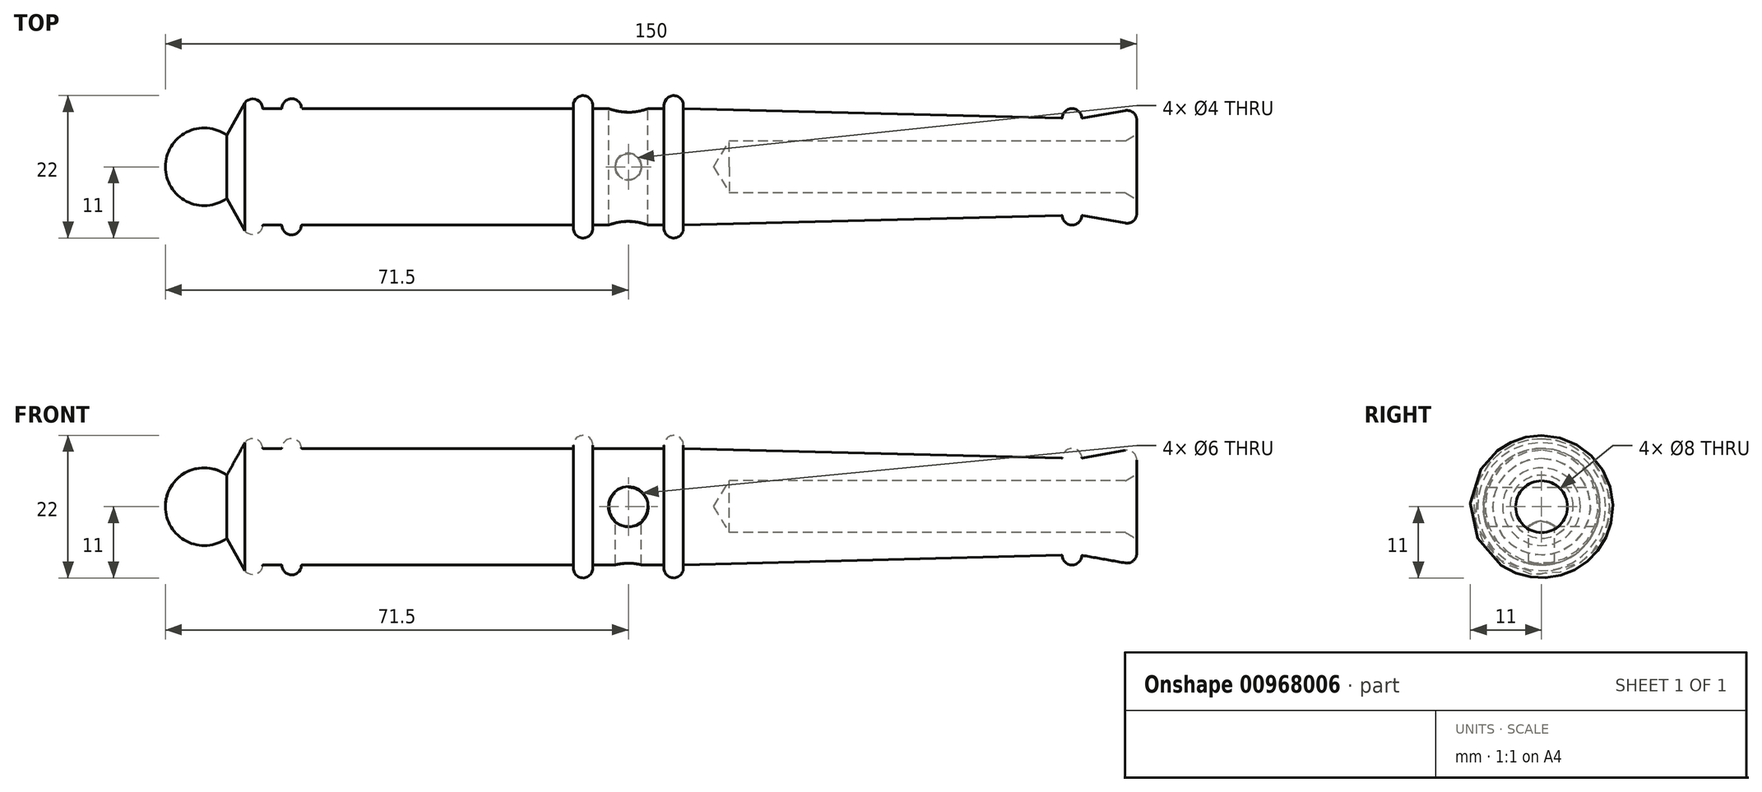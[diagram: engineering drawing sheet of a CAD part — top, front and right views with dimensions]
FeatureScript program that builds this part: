
annotation { "Feature Type Name" : "Feature", "Feature Type Description" : "" }
export const myFeature = defineFeature(function(context is Context, id is Id, definition is map)
    precondition{}
    {
        {
            var Q0;
            Q0=qCreatedBy(makeId("Front.planeOp"),FACE);
            var sketch = newSketch(context, id + "F0", { "sketchPlane" : qUnion([Q0])});
            skLineSegment(sketch, "E0", {"start": v(0, 4) * mm, "end": v(0, 9) * mm});
            skLineSegment(sketch, "E1", {"start": v(-150, 0) * mm, "end": v(-65.36, 0) * mm});
            skArc(sketch, "E2", {"start": v(-70, 9.5) * mm, "mid": v(-71.5, 11) * mm, "end": v(-73, 9.5) * mm});
            skLineSegment(sketch, "E3", {"start": v(-73, 9.5) * mm, "end": v(-73, 9) * mm});
            skLineSegment(sketch, "E4", {"start": v(-70, 9.5) * mm, "end": v(-70, 9) * mm});
            skLineSegment(sketch, "E5.trimOffspring", {"start": v(-73, 9) * mm, "end": v(-84, 9) * mm});
            skLineSegment(sketch, "E6.1.0.0", {"start": v(-84, 9.5) * mm, "end": v(-84, 9) * mm});
            skArc(sketch, "E6.1.0.1", {"start": v(-84, 9.5) * mm, "mid": v(-85.5, 11) * mm, "end": v(-87, 9.5) * mm});
            skLineSegment(sketch, "E6.1.0.2", {"start": v(-87, 9.5) * mm, "end": v(-87, 9) * mm});
            skLineSegment(sketch, "E7.trimOffspring", {"start": v(-87, 9) * mm, "end": v(-129, 9) * mm});
            skLineSegment(sketch, "E8", {"start": v(0, 9) * mm, "end": v(-8.5, 7.5) * mm});
            skLineSegment(sketch, "E9", {"start": v(-8.5, 7.5) * mm, "end": v(-8.5, 7.5) * mm});
            skArc(sketch, "E10", {"start": v(-8.5, 7.5) * mm, "mid": v(-10, 9) * mm, "end": v(-11.5, 7.5) * mm});
            skPoint(sketch, "E11.orphan", {"position": v(-8.5, 9) * mm});
            skPoint(sketch, "E12.orphan", {"position": v(-11.5, 9.38) * mm});
            skLineSegment(sketch, "E13", {"start": v(-70, 9) * mm, "end": v(-11.5, 7.5) * mm});
            skPoint(sketch, "E14.end.orphan", {"position": v(-11.5, 0) * mm});
            skPoint(sketch, "E15.trimOffspring.end.orphan", {"position": v(-8.26, 7.5) * mm});
            skArc(sketch, "E16", {"start": v(-140.5, 4.87) * mm, "mid": v(-146.74, 5.34) * mm, "end": v(-150, 0) * mm});
            skLineSegment(sketch, "E17", {"start": v(-132, 9.04) * mm, "end": v(-132, 9) * mm});
            skLineSegment(sketch, "E18", {"start": v(-129, 9.04) * mm, "end": v(-129, 9) * mm});
            skArc(sketch, "E19", {"start": v(-129, 9) * mm, "mid": v(-130.5, 10.52) * mm, "end": v(-132, 9) * mm});
            skPoint(sketch, "E20.orphan", {"position": v(-129, 10.5) * mm});
            skLineSegment(sketch, "E21.trimOffspring", {"start": v(-132, 9) * mm, "end": v(-135, 9) * mm});
            skPoint(sketch, "E22.orphan", {"position": v(-122.37, 10.5) * mm});
            skLineSegment(sketch, "E23", {"start": v(-140.5, 4.87) * mm, "end": v(-140.5, 4.87) * mm});
            skArc(sketch, "E24", {"start": v(-135, 9.04) * mm, "mid": v(-136.06, 10.44) * mm, "end": v(-137.73, 9.87) * mm});
            skPoint(sketch, "E25.orphan", {"position": v(-138, 10.75) * mm});
            skPoint(sketch, "E26.orphan", {"position": v(-135, 0) * mm});
            skLineSegment(sketch, "E27.trimOffspring", {"start": v(-135, 9.04) * mm, "end": v(-135, 9) * mm});
            skLineSegment(sketch, "E28", {"start": v(-140.5, 4.87) * mm, "end": v(-137.73, 9.87) * mm});
            skPoint(sketch, "E29.orphan", {"position": v(-140.5, 0) * mm});
            skPoint(sketch, "E30.start.orphan", {"position": v(-150, 9) * mm});
            skLineSegment(sketch, "E31", {"start": v(0, 4) * mm, "end": v(-62.9, 4) * mm});
            skLineSegment(sketch, "E32", {"start": v(-62.9, 4) * mm, "end": v(-65.36, 0) * mm});
            skSolve(sketch);
        }
        {
            var Q0;
            Q0=makeQuery(id+"F0.imprint","IMPRINT",FACE,{"disambiguationData":[TD([[makeQuery(id+"F0.imprint","IMPRINT",EDGE,{"derivedFrom":sQuery(id+"F0.wireOp",EDGE,"E0")}),1.0]])]});
            var Q1;
            Q1=sQuery(id+"F0.wireOp",EDGE,"E1");
            revolve(context, id + "F1", {"surfaceOperationType" : NewSurfaceOperationType.NEW, "entities" : qUnion([Q0]), "axis" : qUnion([Q1]), "revolveType" : RevolveType.FULL});
        }
        {
            var Q0;
            Q0=makeQuery(id+"F1.opRevolve","SWEPT_EDGE",EDGE,{"disambiguationData":[OSD([sQuery(id+"F0.wireOp",EDGE,"E0"),sQuery(id+"F0.wireOp",EDGE,"E8")])]});
            fillet(context, id + "F2", {"entities" : qUnion([Q0]), "radius" : 1.5 * mm, "tangentPropagation" : true, "allowEdgeOverflow" : false});
        }
        {
            var Q0;
            Q0=makeQuery(id+"F1.opRevolve","SWEPT_EDGE",EDGE,{"disambiguationData":[OSD([sQuery(id+"F0.wireOp",EDGE,"E0"),sQuery(id+"F0.wireOp",EDGE,"E31")])]});
            chamfer(context, id + "F3", {"entities" : qUnion([Q0]), "chamferType" : ChamferType.OFFSET_ANGLE, "width" : 1 * mm, "oppositeDirection" : false, "angle" : 60 * degree, "tangentPropagation" : true});
        }
        {
            var Q0;
            Q0=qCreatedBy(makeId("Front.planeOp"),FACE);
            var sketch = newSketch(context, id + "F4", { "sketchPlane" : qUnion([Q0])});
            skCircle(sketch, "E33", {"center": v(-78.5, 0) * mm, "radius": 3 * mm});
            skSolve(sketch);
        }
        {
            var Q0;
            Q0 = qSketchRegion(id + "F4", true);
            extrude(context, id + "F5", {"entities" : qUnion([Q0]), "operationType" : NewBodyOperationType.REMOVE, "endBound" : BoundingType.SYMMETRIC, "depth" : 25 * mm, "offsetDistance" : 25 * mm});
        }
        {
            var Q0;
            Q0=qCreatedBy(makeId("Top.planeOp"),FACE);
            var sketch = newSketch(context, id + "F6", { "sketchPlane" : qUnion([Q0])});
            skCircle(sketch, "E34", {"center": v(-78.5, 0) * mm, "radius": 2 * mm});
            skSolve(sketch);
        }
        {
            var Q0;
            Q0 = qSketchRegion(id + "F6", true);
            extrude(context, id + "F7", {"entities" : qUnion([Q0]), "operationType" : NewBodyOperationType.REMOVE, "oppositeDirection" : true, "depth" : 25 * mm, "offsetDistance" : 25 * mm});
        }
        {
            var Q0;
            Q0=makeQuery(id+"F5.boolean.opBoolean","INTERSECT",EDGE,{"disambiguationData":[OD(0.0)],"derivedFrom":[makeQuery(id+"F1.opRevolve","SWEPT_FACE",FACE,{"disambiguationData":[OSD([sQuery(id+"F0.wireOp",EDGE,"E5.trimOffspring")])]}),makeQuery(id+"F5.opExtrude","SWEPT_FACE",FACE,{"disambiguationData":[OSD([sQuery(id+"F4.wireOp",EDGE,"E33")])]})]});
            var Q1;
            Q1=makeQuery(id+"F5.boolean.opBoolean","INTERSECT",EDGE,{"disambiguationData":[OD(1.0)],"derivedFrom":[makeQuery(id+"F1.opRevolve","SWEPT_FACE",FACE,{"disambiguationData":[OSD([sQuery(id+"F0.wireOp",EDGE,"E5.trimOffspring")])]}),makeQuery(id+"F5.opExtrude","SWEPT_FACE",FACE,{"disambiguationData":[OSD([sQuery(id+"F4.wireOp",EDGE,"E33")])]})]});
            var Q2;
            Q2=makeQuery(id+"F7.boolean.opBoolean","INTERSECT",EDGE,{"derivedFrom":[makeQuery(id+"F1.opRevolve","SWEPT_FACE",FACE,{"disambiguationData":[OSD([sQuery(id+"F0.wireOp",EDGE,"E5.trimOffspring")])]}),makeQuery(id+"F7.opExtrude","SWEPT_FACE",FACE,{"disambiguationData":[OSD([sQuery(id+"F6.wireOp",EDGE,"E34")])]})]});
            var Q3;
            Q3=makeQuery(id+"F7.boolean.opBoolean","INTERSECT",EDGE,{"derivedFrom":[makeQuery(id+"F5.boolean.opBoolean","COPY",FACE,{"derivedFrom":makeQuery(id+"F5.opExtrude","SWEPT_FACE",FACE,{"disambiguationData":[OSD([sQuery(id+"F4.wireOp",EDGE,"E33")])]})}),makeQuery(id+"F7.opExtrude","SWEPT_FACE",FACE,{"disambiguationData":[OSD([sQuery(id+"F6.wireOp",EDGE,"E34")])]})]});
            fillet(context, id + "F8", {"entities" : qUnion([Q0, Q1, Q2, Q3]), "radius" : .1 * mm, "tangentPropagation" : true, "allowEdgeOverflow" : false});
        }
        {
            var Q0;
            Q0=makeQuery(id+"F1.opRevolve","SWEPT_EDGE",EDGE,{"disambiguationData":[OSD([sQuery(id+"F0.wireOp",EDGE,"E4"),sQuery(id+"F0.wireOp",EDGE,"E13")])]});
            var Q1;
            Q1=makeQuery(id+"F1.opRevolve","SWEPT_EDGE",EDGE,{"disambiguationData":[OSD([sQuery(id+"F0.wireOp",EDGE,"E5.trimOffspring"),sQuery(id+"F0.wireOp",EDGE,"E6.1.0.0")])]});
            var Q2;
            Q2=makeQuery(id+"F1.opRevolve","SWEPT_EDGE",EDGE,{"disambiguationData":[OSD([sQuery(id+"F0.wireOp",EDGE,"E3"),sQuery(id+"F0.wireOp",EDGE,"E5.trimOffspring")])]});
            var Q3;
            Q3=makeQuery(id+"F1.opRevolve","SWEPT_EDGE",EDGE,{"disambiguationData":[OSD([sQuery(id+"F0.wireOp",EDGE,"E6.1.0.2"),sQuery(id+"F0.wireOp",EDGE,"E7.trimOffspring")])]});
            var Q4;
            Q4=makeQuery(id+"F1.opRevolve","SWEPT_EDGE",EDGE,{"disambiguationData":[OSD([sQuery(id+"F0.wireOp",EDGE,"E10"),sQuery(id+"F0.wireOp",EDGE,"E13")])]});
            var Q5;
            Q5=makeQuery(id+"F1.opRevolve","SWEPT_EDGE",EDGE,{"disambiguationData":[OSD([sQuery(id+"F0.wireOp",EDGE,"E8"),sQuery(id+"F0.wireOp",EDGE,"E10")])]});
            var Q6;
            {var subQ0=sQuery(id+"F0.wireOp",EDGE,"E0");Q6=makeQuery(id+"F3.opChamfer","BLEND_EDGE",EDGE,{"blendedFrom":[makeQuery(id+"F1.opRevolve","SWEPT_EDGE",EDGE,{"disambiguationData":[OSD([subQ0,sQuery(id+"F0.wireOp",EDGE,"E31")])]}),makeQuery(id+"F1.opRevolve","SWEPT_FACE",FACE,{"disambiguationData":[OSD([subQ0])]})],"blendedInto":[makeQuery(id+"F1.opRevolve","SWEPT_FACE",FACE,{"disambiguationData":[OSD([subQ0])]})]});}
            var Q7;
            {var subQ0=sQuery(id+"F0.wireOp",EDGE,"E31");Q7=makeQuery(id+"F3.opChamfer","BLEND_EDGE",EDGE,{"blendedFrom":[makeQuery(id+"F1.opRevolve","SWEPT_EDGE",EDGE,{"disambiguationData":[OSD([sQuery(id+"F0.wireOp",EDGE,"E0"),subQ0])]}),makeQuery(id+"F1.opRevolve","SWEPT_FACE",FACE,{"disambiguationData":[OSD([subQ0])]})],"blendedInto":[makeQuery(id+"F1.opRevolve","SWEPT_FACE",FACE,{"disambiguationData":[OSD([subQ0])]})]});}
            var Q8;
            Q8=makeQuery(id+"F1.opRevolve","SWEPT_EDGE",EDGE,{"disambiguationData":[OSD([sQuery(id+"F0.wireOp",EDGE,"E7.trimOffspring"),sQuery(id+"F0.wireOp",EDGE,"E19")])]});
            var Q9;
            Q9=makeQuery(id+"F1.opRevolve","SWEPT_EDGE",EDGE,{"disambiguationData":[OSD([sQuery(id+"F0.wireOp",EDGE,"E21.trimOffspring"),sQuery(id+"F0.wireOp",EDGE,"E27.trimOffspring")])]});
            var Q10;
            Q10=makeQuery(id+"F1.opRevolve","SWEPT_EDGE",EDGE,{"disambiguationData":[OSD([sQuery(id+"F0.wireOp",EDGE,"E19"),sQuery(id+"F0.wireOp",EDGE,"E21.trimOffspring")])]});
            fillet(context, id + "F9", {"entities" : qUnion([Q0, Q1, Q2, Q3, Q4, Q5, Q6, Q7, Q8, Q9, Q10]), "radius" : .1 * mm, "tangentPropagation" : true, "allowEdgeOverflow" : false});
        }
    });
